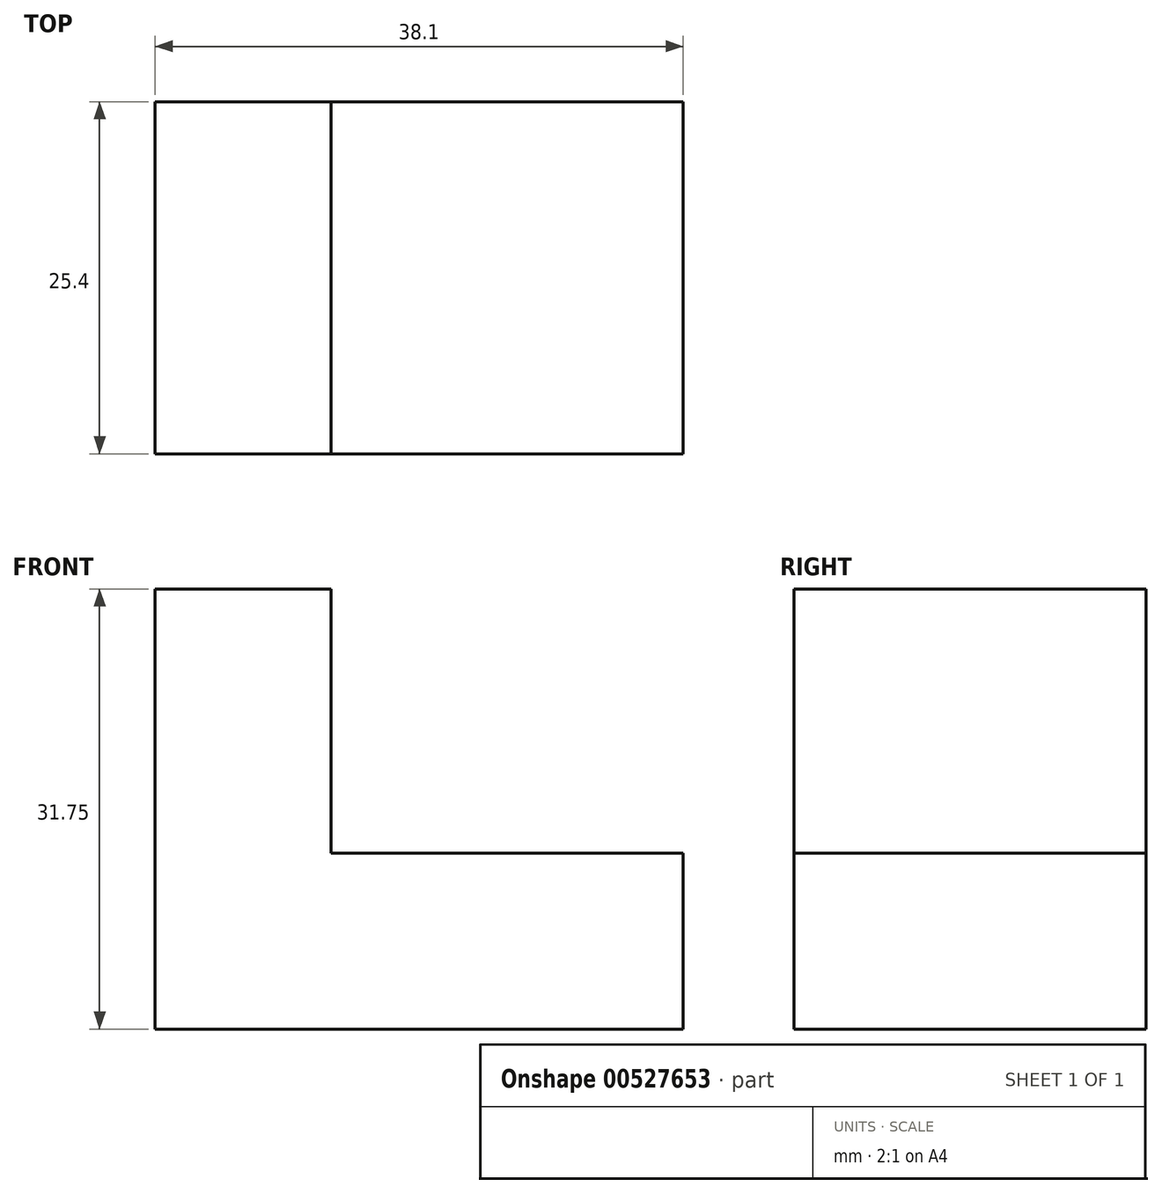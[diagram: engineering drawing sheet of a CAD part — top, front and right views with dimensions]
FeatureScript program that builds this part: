
annotation { "Feature Type Name" : "Feature", "Feature Type Description" : "" }
export const myFeature = defineFeature(function(context is Context, id is Id, definition is map)
    precondition{}
    {
        {
            var Q0;
            Q0=qCreatedBy(makeId("Front.planeOp"),FACE);
            var sketch = newSketch(context, id + "F0", { "sketchPlane" : qUnion([Q0])});
            skLineSegment(sketch, "E0", {"start": v(0, 0) * mm, "end": v(0, 31.75) * mm});
            skLineSegment(sketch, "E1", {"start": v(0, 0) * mm, "end": v(38.1, 0) * mm});
            skLineSegment(sketch, "E2", {"start": v(38.1, 0) * mm, "end": v(38.1, 12.7) * mm});
            skLineSegment(sketch, "E3", {"start": v(38.1, 12.7) * mm, "end": v(12.7, 12.7) * mm});
            skLineSegment(sketch, "E4", {"start": v(12.7, 12.7) * mm, "end": v(12.7, 31.75) * mm});
            skLineSegment(sketch, "E5", {"start": v(12.7, 31.75) * mm, "end": v(0, 31.75) * mm});
            skSolve(sketch);
        }
        {
            var Q0;
            Q0=makeQuery(id+"F0.imprint","IMPRINT",FACE,{"disambiguationData":[TD([[makeQuery(id+"F0.imprint","IMPRINT",EDGE,{"derivedFrom":sQuery(id+"F0.wireOp",EDGE,"E0")}),-1.0]])]});
            extrude(context, id + "F1", {"entities" : qUnion([Q0]), "depth" : 25.4 * mm, "offsetDistance" : 25.4 * mm});
        }
    });
